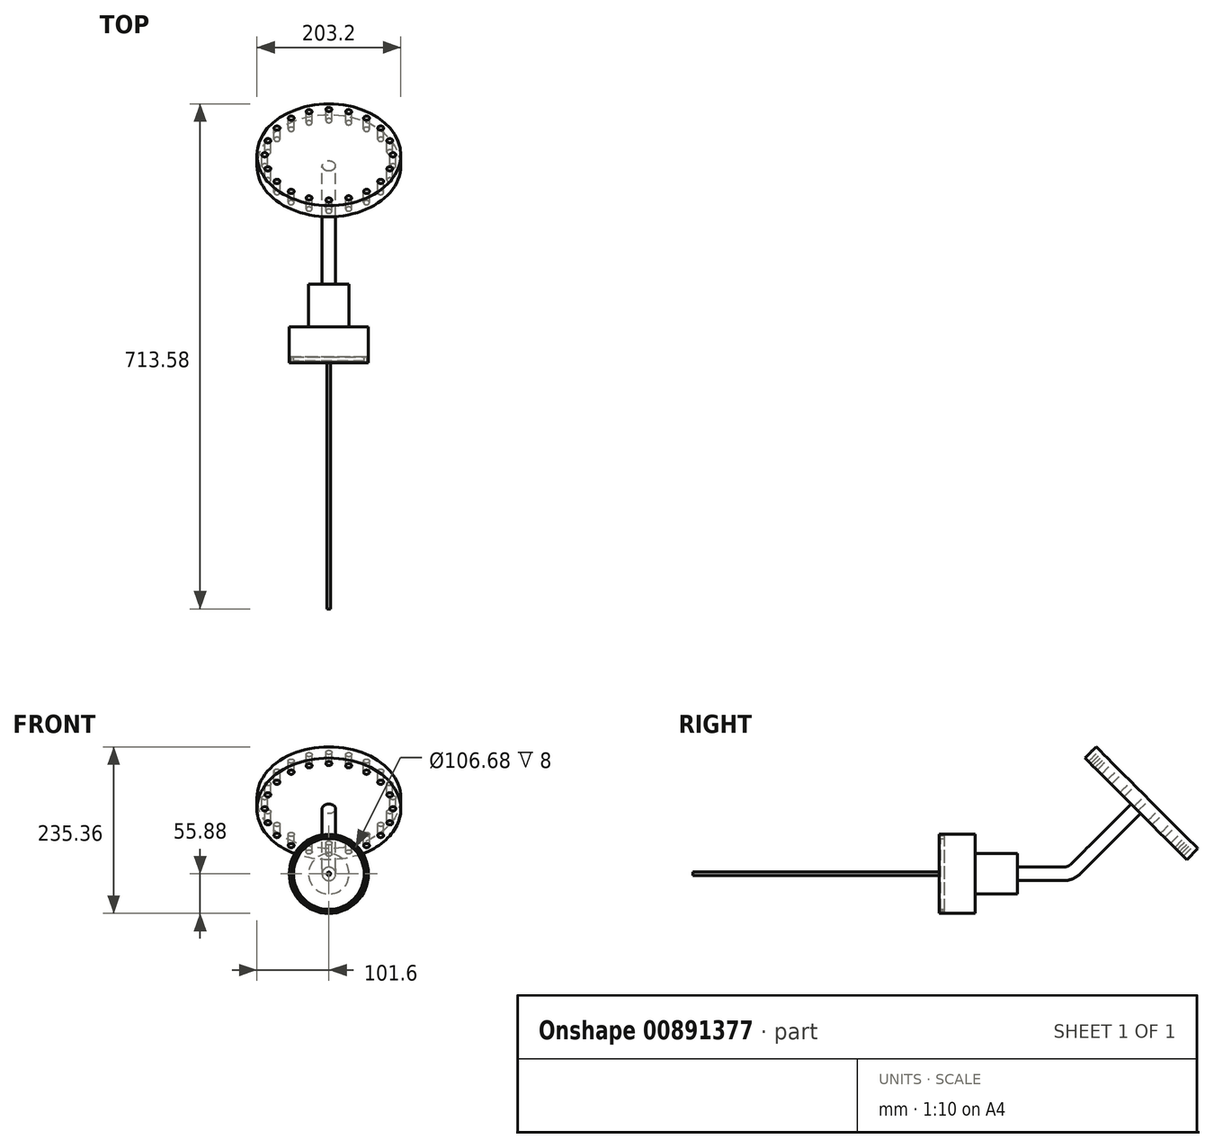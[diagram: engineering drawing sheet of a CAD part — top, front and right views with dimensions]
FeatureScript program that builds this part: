
annotation { "Feature Type Name" : "Feature", "Feature Type Description" : "" }
export const myFeature = defineFeature(function(context is Context, id is Id, definition is map)
    precondition{}
    {
        {
            var Q0;
            Q0=qCreatedBy(makeId("Front.planeOp"),FACE);
            var sketch = newSketch(context, id + "F0", { "sketchPlane" : qUnion([Q0])});
            skCircle(sketch, "E0", {"center": v(0, 0) * mm, "radius": 55.88 * mm});
            skSolve(sketch);
        }
        {
            var Q0;
            Q0 = qSketchRegion(id + "F0", true);
            extrude(context, id + "F1", {"entities" : qUnion([Q0]), "oppositeDirection" : true, "depth" : 50.8 * mm, "offsetDistance" : 25 * mm});
        }
        {
            var Q0;
            Q0=makeQuery(id+"F1.opExtrude","CAP_FACE",FACE,{"disambiguationData":[OSD([sQuery(id+"F0.wireOp",EDGE,"E0")])],"isStart":false});
            var sketch = newSketch(context, id + "F2", { "sketchPlane" : qUnion([Q0])});
            skCircle(sketch, "E1", {"center": v(0, 0) * mm, "radius": 28.58 * mm});
            skSolve(sketch);
        }
        {
            var Q0;
            Q0 = qSketchRegion(id + "F2", true);
            extrude(context, id + "F3", {"entities" : qUnion([Q0]), "operationType" : NewBodyOperationType.ADD, "depth" : 110.74 * mm - 50.8 * mm, "offsetDistance" : 25 * mm});
        }
        {
            var Q0;
            Q0=qCreatedBy(makeId("Right.planeOp"),FACE);
            var sketch = newSketch(context, id + "F4", { "sketchPlane" : qUnion([Q0])});
            skLineSegment(sketch, "E2", {"start": v(108.26, 0) * mm, "end": v(175.74, 0) * mm});
            skLineSegment(sketch, "E3", {"start": v(193.42, 7.32) * mm, "end": v(278.02, 91.92) * mm});
            skPoint(sketch, "E4.visualSharp", {"position": v(186.1, 0) * mm});
            skArc(sketch, "E4.filletArc", {"start": v(175.74, 0) * mm, "mid": v(185.31, 1.9) * mm, "end": v(193.42, 7.32) * mm});
            skSolve(sketch);
        }
        {
            var Q0;
            Q0=makeQuery(id+"F3.opExtrude","CAP_FACE",FACE,{"disambiguationData":[OSD([sQuery(id+"F2.wireOp",EDGE,"E1")])],"isStart":false});
            var sketch = newSketch(context, id + "F5", { "sketchPlane" : qUnion([Q0])});
            skCircle(sketch, "E5", {"center": v(0, 0) * mm, "radius": 9.53 * mm});
            skSolve(sketch);
        }
        {
            var Q0;
            Q0=makeQuery(id+"F5.imprint","IMPRINT",FACE,{"disambiguationData":[TD([[makeQuery(id+"F5.imprint","IMPRINT",EDGE,{"derivedFrom":sQuery(id+"F5.wireOp",EDGE,"E5")}),1.0]])]});
            var Q1;
            Q1 = qConstructionFilter(qBodyType(qCreatedBy(id + "F4" ,EDGE), BodyType.WIRE), ConstructionObject.NO);
            sweep(context, id + "F6", {"operationType" : NewBodyOperationType.ADD, "profiles" : qUnion([Q0]), "path" : qUnion([Q1])});
        }
        {
            var Q0;
            Q0=makeQuery(id+"F6.opSweep","CAP_FACE",FACE,{"disambiguationData":[OSD([sQuery(id+"F4.wireOp",VERTEX,"E3.end"),sQuery(id+"F5.wireOp",EDGE,"E5")])],"isStart":false});
            var sketch = newSketch(context, id + "F7", { "sketchPlane" : qUnion([Q0])});
            skCircle(sketch, "E6", {"center": v(0, -131.6) * mm, "radius": 101.6 * mm});
            skSolve(sketch);
        }
        {
            var Q0;
            Q0 = qSketchRegion(id + "F7", true);
            extrude(context, id + "F8", {"entities" : qUnion([Q0]), "operationType" : NewBodyOperationType.ADD, "depth" : 22.22 * mm, "offsetDistance" : 25 * mm});
        }
        {
            var Q0;
            Q0=makeQuery(id+"F8.opExtrude","CAP_FACE",FACE,{"disambiguationData":[OSD([sQuery(id+"F7.wireOp",EDGE,"E6")])],"isStart":false});
            var sketch = newSketch(context, id + "F9", { "sketchPlane" : qUnion([Q0])});
            skCircle(sketch, "E7", {"center": v(0, -222.14) * mm, "radius": 4.2 * mm});
            skCircle(sketch, "E8.1.0", {"center": v(27.98, -217.71) * mm, "radius": 4.2 * mm});
            skCircle(sketch, "E8.2.0", {"center": v(53.22, -204.85) * mm, "radius": 4.2 * mm});
            skCircle(sketch, "E8.3.0", {"center": v(73.26, -184.82) * mm, "radius": 4.2 * mm});
            skCircle(sketch, "E8.4.0", {"center": v(86.12, -159.57) * mm, "radius": 4.2 * mm});
            skCircle(sketch, "E8.5.0", {"center": v(90.55, -131.6) * mm, "radius": 4.2 * mm});
            skCircle(sketch, "E8.6.0", {"center": v(86.12, -103.61) * mm, "radius": 4.2 * mm});
            skCircle(sketch, "E8.7.0", {"center": v(73.26, -78.37) * mm, "radius": 4.2 * mm});
            skCircle(sketch, "E8.8.0", {"center": v(53.22, -58.34) * mm, "radius": 4.2 * mm});
            skCircle(sketch, "E8.9.0", {"center": v(27.98, -45.47) * mm, "radius": 4.2 * mm});
            skCircle(sketch, "E8.10.0", {"center": v(0, -41.04) * mm, "radius": 4.2 * mm});
            skCircle(sketch, "E8.11.0", {"center": v(-27.98, -45.47) * mm, "radius": 4.2 * mm});
            skCircle(sketch, "E8.12.0", {"center": v(-53.22, -58.34) * mm, "radius": 4.2 * mm});
            skCircle(sketch, "E8.13.0", {"center": v(-73.26, -78.37) * mm, "radius": 4.2 * mm});
            skCircle(sketch, "E8.14.0", {"center": v(-86.12, -103.61) * mm, "radius": 4.2 * mm});
            skCircle(sketch, "E8.15.0", {"center": v(-90.55, -131.6) * mm, "radius": 4.2 * mm});
            skCircle(sketch, "E8.16.0", {"center": v(-86.12, -159.57) * mm, "radius": 4.2 * mm});
            skCircle(sketch, "E8.17.0", {"center": v(-73.26, -184.82) * mm, "radius": 4.2 * mm});
            skCircle(sketch, "E8.18.0", {"center": v(-53.22, -204.85) * mm, "radius": 4.2 * mm});
            skCircle(sketch, "E8.19.0", {"center": v(-27.98, -217.71) * mm, "radius": 4.2 * mm});
            skPoint(sketch, "E8.center", {"position": v(0, -131.6) * mm});
            skSolve(sketch);
        }
        {
            var Q0;
            Q0 = qSketchRegion(id + "F9", true);
            extrude(context, id + "F10", {"entities" : qUnion([Q0]), "operationType" : NewBodyOperationType.REMOVE, "endBound" : BoundingType.UP_TO_NEXT, "oppositeDirection" : true, "depth" : 25 * mm, "offsetDistance" : 25 * mm});
        }
        {
            var Q0;
            Q0=makeQuery(id+"F1.opExtrude","CAP_FACE",FACE,{"disambiguationData":[OSD([sQuery(id+"F0.wireOp",EDGE,"E0")])],"isStart":true});
            var sketch = newSketch(context, id + "F11", { "sketchPlane" : qUnion([Q0])});
            skCircle(sketch, "E9", {"center": v(0, 0) * mm, "radius": 53.34 * mm});
            skSolve(sketch);
        }
        {
            var Q0;
            Q0=makeQuery(id+"F11.imprint","IMPRINT",FACE,{"disambiguationData":[TD([[makeQuery(id+"F11.imprint","IMPRINT",EDGE,{"derivedFrom":sQuery(id+"F11.wireOp",EDGE,"E9")}),1.0]])]});
            extrude(context, id + "F12", {"entities" : qUnion([Q0]), "operationType" : NewBodyOperationType.REMOVE, "oppositeDirection" : true, "depth" : 8 * mm, "offsetDistance" : 25 * mm});
        }
        {
            var Q0;
            Q0=makeQuery(id+"F12.boolean.opBoolean","COPY",FACE,{"derivedFrom":makeQuery(id+"F12.opExtrude","CAP_FACE",FACE,{"disambiguationData":[OSD([sQuery(id+"F11.wireOp",EDGE,"E9")])],"isStart":false})});
            var sketch = newSketch(context, id + "F13", { "sketchPlane" : qUnion([Q0])});
            skCircle(sketch, "E10", {"center": v(0, 0) * mm, "radius": 50 * mm});
            skSolve(sketch);
        }
        {
            var Q0;
            Q0 = qSketchRegion(id + "F13", true);
            extrude(context, id + "F14", {"entities" : qUnion([Q0]), "depth" : 6 * mm, "offsetDistance" : 25 * mm});
        }
        {
            var Q0;
            Q0=makeQuery(id+"F14.opExtrude","CAP_FACE",FACE,{"disambiguationData":[OSD([sQuery(id+"F13.wireOp",EDGE,"E10")])],"isStart":false});
            var sketch = newSketch(context, id + "F15", { "sketchPlane" : qUnion([Q0])});
            skCircle(sketch, "E11", {"center": v(0, 0) * mm, "radius": 2.5 * mm});
            skSolve(sketch);
        }
        {
            var Q0;
            Q0 = qSketchRegion(id + "F15", true);
            extrude(context, id + "F16", {"entities" : qUnion([Q0]), "flatOperationType" : FlatOperationType.REMOVE, "depth" : 350 * mm, "offsetDistance" : 25 * mm, "domain" : OperationDomain.MODEL});
        }
    });
